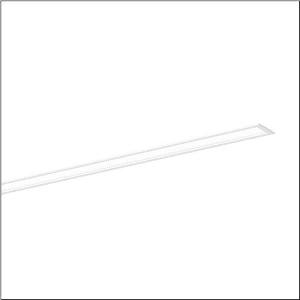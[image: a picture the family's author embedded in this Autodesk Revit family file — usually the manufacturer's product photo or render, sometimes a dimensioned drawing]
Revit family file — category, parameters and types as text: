
# Revit family: silica_r__21_51mx13tat4w_7811
name_source: partatom
category: Lighting Fixtures
units: mm (PartAtom-declared; Revit-internal decimal feet)

## family parameters
Cut with Voids When Loaded = No
Host = Face
Light Source = No
Part Type = Normal
Room Calculation Point = No
Round Connector Dimension = Use Diameter
Shared = No

## types (1)
- --- (1 x LED, 3230 lm, 32.4 W, 6500K)
    Apparent Load = 32 VA
    CIE Flux Codes = 78 96 99 100 100
    Color Rendering = 80
    Color Temperature = 6500K
    Default Elevation = 1800 mm
    Description = Silica® 21, office luminaire, primary optical cover: prismatic diffuser, of PMMA, CAT 2 (L<= 3000cd/m²), light emission: direct distribution, primary light characteristic: symmetric, installation type: recessed, LED, rated luminous flux: 3.230lm, luminous efficacy: 95lm/W, light colour: 8tw, colour temperature: 2700..6500K, with terminal, 3+2-pole, max. 2.5mm², mains connection: 220..240V, AC, 50/60Hz, rated input power: 34W, luminaire housing, of aluminium, traffic white (RAL 9016), length: 1.228mm, width: 79mm, height: 53mm, protection rating (complete): IP20, insulation class (complete): insulation class I (protective earthing), certification: CE, permissible operating ambient temperature: 0..+35°C, standard: EN 50419, packaging unit: 1 piece
    Height = 0 mm  [stored 0 ft]
    Lamp = 1 x LED
    Lamp Light Flux = 3230 lm
    Lamp Power = 32.4 W
    Lamp count = 1
    Length = 1227 mm
    Luminous efficacy = 100 lm/W
    Manufacturer = Siteco
    ModVariant = No
    Model = 51MX13TAT4W
    Mounting Place = Ceiling
    Mounting Type = Recessed
    Number of Poles = 1
    OnlyDefault = Yes
    Power Factor = 1
    Product Name = Silica® 21
    Product group = office luminaire | ceiling recessed
    ProductGroupID = 401
    Protection Class = Protection class I
    Protection Degree = IP 20
    RLX_Detail_Level = 1
    RLX_Emergency_Light_Flux = 0 lm
    RLX_Emergency_Type = 0
    RLX_Emergency_Type_DB = No
    RlxData = <blob elided: 13053 chars, md5=7241f60b>
    Socket = socket
    Standby Power = 0 W
    System Light Flux = 3230 lm
    System Power = 32 W
    Type Comments = individual setting
    Type Image = l_1297733.jpg
    URL = http://relux.com
    VarID = @adj_071179
    Voltage = 0 V
    Weight = 0.00 kg
    Width = 79 mm

note: [stored X ft] marks values corroborated as IEEE doubles in the binary element streams (Revit-internal decimal feet)

## geometry (parser evidence)
native form markers: Sweep x10
no freeform markers — native parametric forms only
